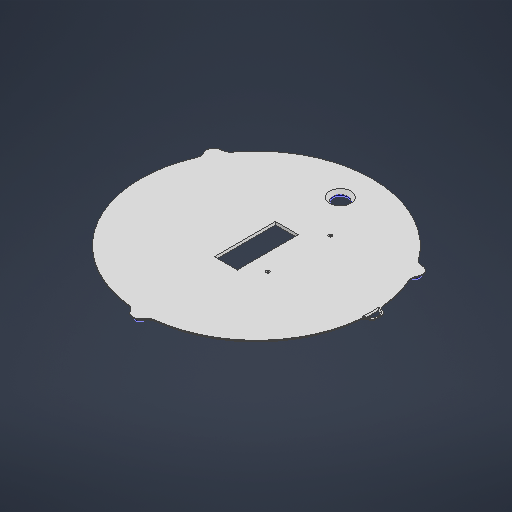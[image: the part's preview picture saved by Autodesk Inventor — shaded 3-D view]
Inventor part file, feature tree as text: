
AUTODESK INVENTOR PART (.ipt)
format: ipt  version: 2025.1 (Build 291241000, 241)  size: 925,184 bytes
history: native  units: mm
features: extrude x8, sketch x4, fillet x4, chamfer x3, pattern_circular x2, shell x1, projected_geometry x1
ambient origin geometry x8: Origin, YZ Plane, XZ Plane, XY Plane, X Axis, Y Axis, Z Axis, Center Point
bodies: Solid1 (feature_tree), Solid2 (feature_tree)
feature tree (23):
  sketch  "Sketch1"  dims[d0=140.0mm d1=10.0mm]
  extrude  "Extrusion1"  Depth=10.0mm
  chamfer  "Chamfer1"  Distance=2.0mm
  fillet  "Fillet1"  Radius=3.2mm
  extrude  "Extrusion5"  Depth=76.0mm
  shell  "Shell1"  Thickness=10.0mm
  fillet  "Fillet4"  Radius=5.0mm
  extrude  "Extrusion6"  Depth=2.0mm TaperAngle=360.0deg
  extrude  "Extrusion7"  Depth=2.0mm
  extrude  "Extrusion8"  TaperAngle=15.0deg  [1 undecoded]
  extrude  "Extrusion10"  Depth=55.0mm
  fillet  "Fillet2"  Radius=5.0mm
  chamfer  "Chamfer5"  Distance=15.0mm
  sketch  "Sketch3"  dims[d25=6.0mm d26=76.0mm d27=10.0mm d30=5.0mm d31=30.0mm d33=360.0deg d35=22.0mm d36=15.0deg d41=55.0mm d42=5.0mm d43=0.0mm d44=15.0mm d45=40.0mm d46=0.8mm d47=0.0mm d48=2.5mm d49=41.0mm d50=0.0mm d51=0.0mm d52=10.0mm d54=4.2mm d55=4.2mm d56=1.0mm d57=0.0mm d60=18.5mm d62=5.0mm d64=10.0mm d65=0.0mm d66=20.071286mm d67=20.071286mm d68=3.0mm d69=1.5mm d70=2.0mm d71=0.8mm d72=2.0mm d73=45.0deg d74=4.4mm d76=1.0mm d77=1.0mm d78=1.0mm d79=1.0mm d80=0.0mm d81=30.0mm d82=360.0deg d84=1.0mm d85=3.0mm d86=1.0mm d87=1.5mm d88=1.0mm d89=0.0mm d90=1.5mm d91=2.0mm d92=45.0deg d93=30.0mm d94=360.0deg]
  extrude  "Extrusion11"  Depth=2.0mm
  extrude  "Extrusion12"  Depth=2.0mm TaperAngle=0.0deg
  fillet  "Fillet3"  Radius=2.5mm
  pattern_circular  "Circular Pattern1"  [2 undecoded]
  chamfer  "Chamfer6"  [1 undecoded]
  pattern_circular  "Circular Pattern2"  [2 undecoded]
  sketch  "Sketch Circular Pattern1"  dims[d2=55.0mm d3=2.0mm d4=0.0mm]
  sketch  "Sketch2"  dims[d5=2.0mm d6=2.0mm d7=45.0deg d9=3.2mm]
  projected_geometry  "Projected Loop1"
note: 6 required parameter values undecoded (feature->parameter linkage not recoverable at this tier; creation-order binding heuristic only, values carry confidence <= 0.55)
